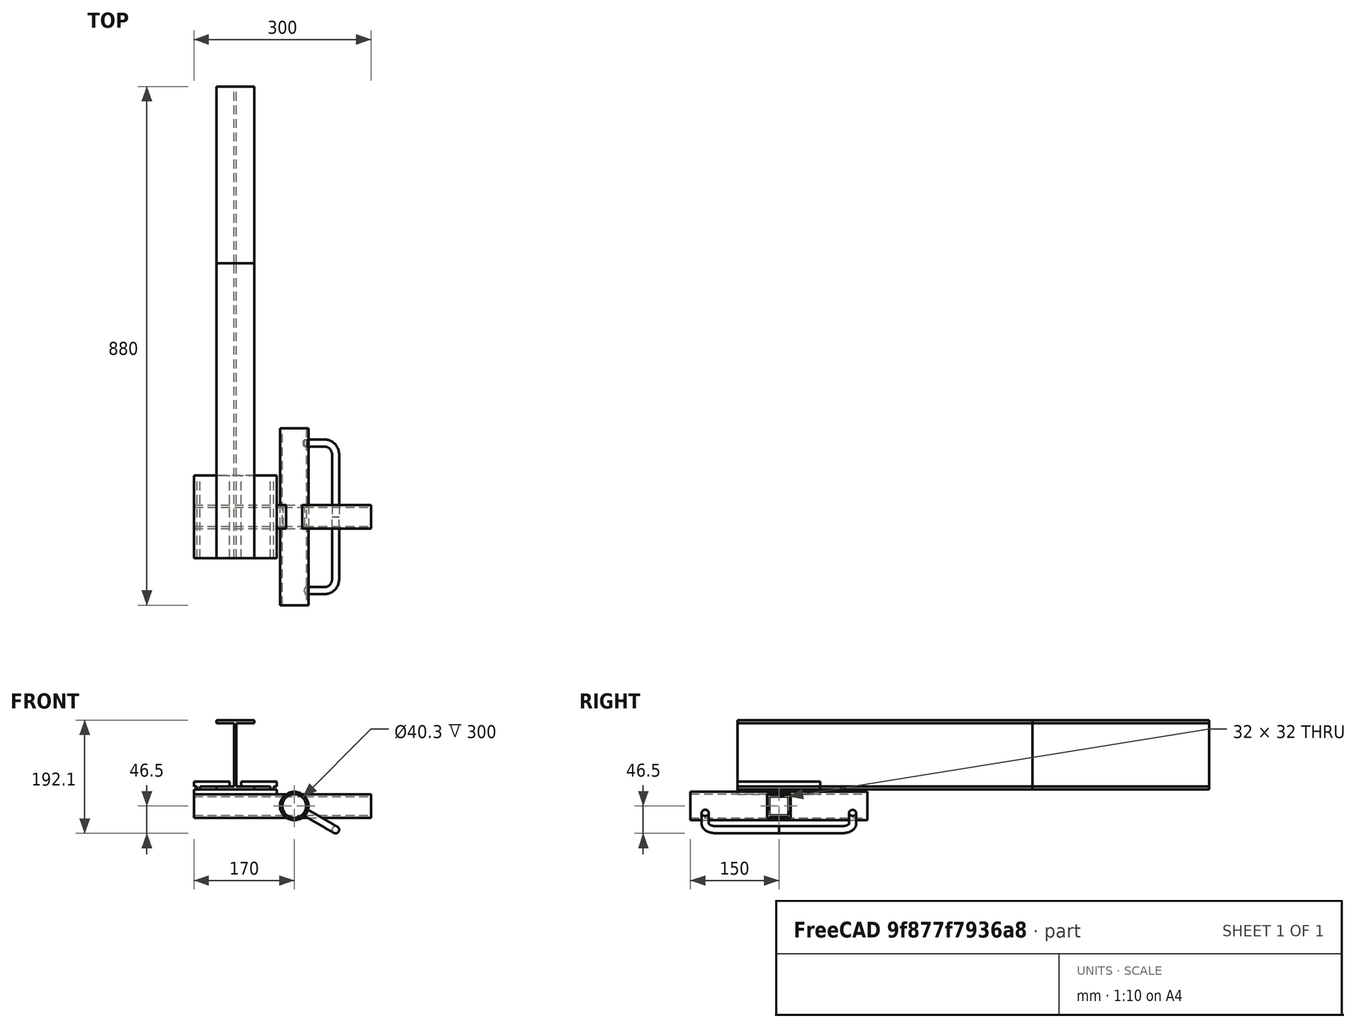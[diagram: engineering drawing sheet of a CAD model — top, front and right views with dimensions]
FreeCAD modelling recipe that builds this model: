
FCSTD DOCUMENT  (FreeCAD 0.21R33771 (Git))
Label: Haltegriff_FEM_RC
License: All rights reserved
LicenseURL: https://en.wikipedia.org/wiki/All_rights_reserved
objects: Part::FeaturePython×8, Sketcher::SketchObject×5, Part::Feature×3, Part::Extrusion×3, Fem::FeaturePython×2, Fem::ConstraintForce×2, Part::Sweep×1, App::DocumentObjectGroup×1, App::MaterialObjectPython×1, Fem::ConstraintFixed×1, Fem::FemSolverObjectPython×1, Fem::FemMeshObjectPython×1, Fem::FemAnalysis×1
note: 20 computed .brp shape members not serialized (recipe doc carries the construction recipe); baked Part::Feature solids carry a one-line shape summary decoded from their .brp

FEATURE [Part::Feature] Defeatured  label="IPEA120"
  shape: bbox 64 x 500 x 117.6 mm, 14 faces (baked)
FEATURE [Part::Feature] Defeatured002  label="IPEA120_2"
  shape: bbox 64 x 300 x 117.6 mm, 14 faces (baked)
FEATURE [Sketcher::SketchObject] Sketch
  ExternalGeometry = -> [Defeatured]
  FullyConstrained = true
  MapMode = 5
  Placement = pos=(0,0,0) rot=(1,0,0;1.5708rad)
  sketch-geometry (4):
    g0: LineSegment StartX=-70 StartY=-58.8 StartZ=0 EndX=-70 EndY=-66.8 EndZ=0
    g1: LineSegment StartX=-70 StartY=-66.8 StartZ=0 EndX=70 EndY=-66.8 EndZ=0
    g2: LineSegment StartX=70 StartY=-66.8 StartZ=0 EndX=70 EndY=-58.8 EndZ=0
    g3: LineSegment StartX=70 StartY=-58.8 StartZ=0 EndX=-70 EndY=-58.8 EndZ=0
  constraints (11):
    c: Coincident(g0,g1)
    c: Coincident(g1,g2)
    c: Coincident(g2,g3)
    c: Coincident(g3,g0)
    c: Vertical(g0)
    c: Vertical(g2)
    c: Horizontal(g3)
    c: Symmetric(g0,g1,g-2)
    c: PointOnObject(g-3,g3)
    c: DistanceY(g2,g2) = 8
    c: DistanceX(g1,g1) = 140
FEATURE [Part::Extrusion] Extrude  label="platte"
  Base = -> Sketch
  Dir = (0,1,0)
  DirMode = 0
  FaceMakerClass = Part::FaceMakerBullseye
  LengthFwd = 140
  LengthRev = 0
  Solid = true
  Symmetric = false
FEATURE [Sketcher::SketchObject] Sketch001
  ExternalGeometry = -> [Extrude,Defeatured]
  FullyConstrained = true
  MapMode = 5
  Placement = pos=(0,0,0) rot=(1,0,0;1.5708rad)
  sketch-geometry (16):
    g0: LineSegment StartX=64.9 StartY=-58.8 StartZ=0 EndX=64.9 EndY=-53.7 EndZ=0
    g1: LineSegment StartX=64.9 StartY=-53.7 StartZ=0 EndX=70 EndY=-53.7 EndZ=0
    g2: LineSegment StartX=70 StartY=-53.7 StartZ=0 EndX=70 EndY=-45.7 EndZ=0
    g3: LineSegment StartX=70 StartY=-45.7 StartZ=0 EndX=10 EndY=-45.7 EndZ=0
    g4: LineSegment StartX=10 StartY=-45.7 StartZ=0 EndX=10 EndY=-53.7 EndZ=0
    g5: LineSegment StartX=10 StartY=-53.7 StartZ=0 EndX=59.8 EndY=-53.7 EndZ=0
    g6: LineSegment StartX=59.8 StartY=-53.7 StartZ=0 EndX=59.8 EndY=-58.8 EndZ=0
    g7: LineSegment StartX=59.8 StartY=-58.8 StartZ=0 EndX=64.9 EndY=-58.8 EndZ=0
    g8: LineSegment StartX=-64.9 StartY=-58.8 StartZ=0 EndX=-64.9 EndY=-53.7 EndZ=0
    g9: LineSegment StartX=-64.9 StartY=-53.7 StartZ=0 EndX=-70 EndY=-53.7 EndZ=0
    g10: LineSegment StartX=-70 StartY=-53.7 StartZ=0 EndX=-70 EndY=-45.7 EndZ=0
    g11: LineSegment StartX=-70 StartY=-45.7 StartZ=0 EndX=-10 EndY=-45.7 EndZ=0
    g12: LineSegment StartX=-10 StartY=-45.7 StartZ=0 EndX=-10 EndY=-53.7 EndZ=0
    g13: LineSegment StartX=-10 StartY=-53.7 StartZ=0 EndX=-59.8 EndY=-53.7 EndZ=0
    g14: LineSegment StartX=-59.8 StartY=-53.7 StartZ=0 EndX=-59.8 EndY=-58.8 EndZ=0
    g15: LineSegment StartX=-59.8 StartY=-58.8 StartZ=0 EndX=-64.9 EndY=-58.8 EndZ=0
  constraints (48):
    c: Coincident(g0,g1)
    c: Coincident(g1,g2)
    c: Vertical(g2)
    c: Coincident(g2,g3)
    c: Horizontal(g3)
    c: Coincident(g3,g4)
    c: Vertical(g4)
    c: Coincident(g4,g5)
    c: Horizontal(g5)
    c: Coincident(g5,g6)
    c: Vertical(g6)
    c: Coincident(g6,g7)
    c: Coincident(g7,g0)
    c: Coincident(g8,g9)
    c: Coincident(g9,g10)
    c: Vertical(g10)
    c: Coincident(g10,g11)
    c: Horizontal(g11)
    c: Coincident(g11,g12)
    c: Coincident(g12,g13)
    c: Horizontal(g13)
    c: Coincident(g13,g14)
    c: Coincident(g14,g15)
    c: Coincident(g15,g8)
    c: Horizontal(g15)
    c: Vertical(g8)
    c: Vertical(g14)
    c: Horizontal(g9)
    c: Horizontal(g8,g13)
    c: PointOnObject(g-6,g13)
    c: Horizontal(g-4,g8)
    c: Vertical(g-4,g9)
    c: Equal(g-4,g10)
    c: Equal(g14,g15)
    c: Equal(g8,g9)
    c: Vertical(g12)
    c: DistanceX(g11,g11) = 60
    c: Horizontal(g7)
    c: Horizontal(g0,g-3)
    c: Vertical(g0)
    c: Horizontal(g0,g5)
    c: PointOnObject(g-5,g5)
    c: Equal(g12,g2)
    c: Equal(g3,g11)
    c: Horizontal(g1)
    c: Vertical(g1,g-3)
    c: Equal(g1,g7)
    c: Equal(g7,g0)
FEATURE [Part::Extrusion] Extrude001  label="platte001"
  Base = -> Sketch001
  Dir = (0,1,0)
  DirMode = 0
  FaceMakerClass = Part::FaceMakerBullseye
  LengthFwd = 140
  LengthRev = 0
  Solid = true
  Symmetric = false
FEATURE [Part::Feature] Defeatured003  label="QR40x4"
  shape: bbox 300 x 40 x 40 mm, 10 faces (baked)
FEATURE [Sketcher::SketchObject] Sketch002
  FullyConstrained = true
  Placement = pos=(0,0,0) rot=(1,0,0;1.5708rad)
  sketch-geometry (3):
    g0: Circle CenterX=0 CenterY=0 CenterZ=0 NormalX=0 NormalY=0 NormalZ=1 AngleXU=0 Radius=24.15
    g1: Circle CenterX=0 CenterY=0 CenterZ=0 NormalX=0 NormalY=0 NormalZ=1 AngleXU=0 Radius=20.15
    g2: LineSegment StartX=20.15 StartY=0 StartZ=0 EndX=24.15 EndY=0 EndZ=0
  constraints (8):
    c: Diameter(g0) = 48.3
    c: Coincident(g0,g-1)
    c: Coincident(g1,g0)
    c: PointOnObject(g2,g1)
    c: PointOnObject(g2,g0)
    c: PointOnObject(g2,g-1)
    c: Horizontal(g2)
    c: DistanceX(g2,g2) = 4
FEATURE [Part::Extrusion] Extrude002  label="R48x4"
  Base = -> Sketch002
  Dir = (0,-1,2e-16)
  DirMode = 2
  FaceMakerClass = Part::FaceMakerBullseye
  LengthFwd = 80
  LengthRev = 220
  Placement = pos=(100,1.42e-14,-86.8) rot=(0,0,1;0rad)
  Solid = true
  Symmetric = false
FEATURE [Sketcher::SketchObject] Sketch003
  ExternalGeometry = -> [Extrude002]
  FullyConstrained = true
  sketch-geometry (10):
    g0: LineSegment StartX=0 StartY=195 StartZ=0 EndX=40 EndY=195 EndZ=0
    g1: LineSegment StartX=0 StartY=-55 StartZ=0 EndX=40 EndY=-55 EndZ=0
    g2: LineSegment StartX=60 StartY=175 StartZ=0 EndX=60 EndY=120 EndZ=0
    g3: LineSegment StartX=60 StartY=20 StartZ=0 EndX=60 EndY=-35 EndZ=0
    g4: ArcOfCircle CenterX=40 CenterY=175 CenterZ=0 NormalX=0 NormalY=0 NormalZ=1 AngleXU=0 Radius=20 StartAngle=0 EndAngle=1.5708
    g5: ArcOfCircle CenterX=40 CenterY=-35 CenterZ=0 NormalX=0 NormalY=0 NormalZ=1 AngleXU=0 Radius=20 StartAngle=4.71239 EndAngle=6.28319
    g6: LineSegment StartX=60 StartY=120 StartZ=0 EndX=60 EndY=70 EndZ=0
    g7: LineSegment StartX=60 StartY=70 StartZ=0 EndX=60 EndY=20 EndZ=0
    g8: LineSegment StartX=120.15 StartY=220 StartZ=0 EndX=0 EndY=195 EndZ=0
    g9: LineSegment StartX=120.15 StartY=-80 StartZ=0 EndX=0 EndY=-55 EndZ=0
  constraints (31):
    c: Horizontal(g0)
    c: Horizontal(g1)
    c: Vertical(g2)
    c: Coincident(g6,g2)
    c: Vertical(g3)
    c: Coincident(g7,g3)
    c: Equal(g2,g3)
    c: DistanceY(g7,g6) = 100
    c: Vertical(g0,g1)
    c: Vertical(g0,g1)
    c: DistanceY(g1,g0) = 250
    c: Coincident(g4,g0)
    c: Coincident(g4,g2)
    c: Coincident(g5,g3)
    c: Coincident(g5,g1)
    c: Vertical(g5,g1)
    c: Horizontal(g5,g3)
    c: Vertical(g4,g0)
    c: Horizontal(g4,g2)
    c: Radius(g4) = 20
    c: DistanceX(g0,g2) = 60
    c: Coincident(g6,g7)
    c: Vertical(g6)
    c: Vertical(g7)
    c: Equal(g6,g7)
    c: PointOnObject(g1,g-2)
    c: Coincident(g8,g-3)
    c: Coincident(g8,g0)
    c: Coincident(g9,g-3)
    c: Coincident(g9,g1)
    c: Equal(g9,g8)
FEATURE [Sketcher::SketchObject] Sketch004
  ExternalGeometry = -> [Sketch003]
  FullyConstrained = true
  Placement = pos=(0,0,0) rot=(0.57735,0.57735,0.57735;2.0944rad)
  sketch-geometry (1):
    g0: Circle CenterX=-55 CenterY=0 CenterZ=0 NormalX=0 NormalY=0 NormalZ=1 AngleXU=0 Radius=6
  constraints (2):
    c: Coincident(g0,g-3)
    c: Diameter(g0) = 12
FEATURE [Part::Sweep] Sweep
  Frenet = true
  Placement = pos=(118.187,1.4e-14,-97.3) rot=(0,1,0;0.523599rad)
  Sections = -> [Sketch004]
  Solid = true
  Spine = -> Sketch003 [Edge1,Edge2,Edge3,Edge4]
  Transition = 1
FEATURE [Part::FeaturePython] Clone  label="Sweep001"  # Draft clone (typed FeaturePython)
  AttacherType = Attacher::AttachEngine3D
  Fuse = false
  Objects = -> [Sweep]
  Placement = pos=(118.187,140,-97.3) rot=(0.965926,0,-0.258819;3.14159rad)
  Scale = (1,1,1)
FEATURE [Part::FeaturePython] Facebinder  # WARN: FeaturePython — macro-defined, semantics opaque (R4)
  Area = 45521.7
  Extrusion = 0
  Faces = -> [Extrude002]
  RemoveSplitter = false
  Sew = false
FEATURE [Part::FeaturePython] Slice  # WARN: FeaturePython — macro-defined, semantics opaque (R4)
  Base = -> Defeatured003
  Mode = 1
  Tolerance = 0
  Tools = -> [Facebinder]
FEATURE [Part::FeaturePython] Slice_child0  label="Slice.0"  # WARN: FeaturePython — macro-defined, semantics opaque (R4)
  Base = -> Slice
  FilterType = 1
  Invert = false
  OverrideMaxVal = 0
  WindowFrom = 80
  WindowTo = 100
  items = 0
FEATURE [Part::FeaturePython] Slice_child1  label="Slice.1"  # WARN: FeaturePython — macro-defined, semantics opaque (R4)
  Base = -> Slice
  FilterType = 1
  Invert = false
  OverrideMaxVal = 0
  WindowFrom = 80
  WindowTo = 100
  items = 1
FEATURE [Part::FeaturePython] Slice_child2  label="Slice.2"  # WARN: FeaturePython — macro-defined, semantics opaque (R4)
  Base = -> Slice
  FilterType = 1
  Invert = false
  OverrideMaxVal = 0
  WindowFrom = 80
  WindowTo = 100
  items = 2
FEATURE [App::DocumentObjectGroup] GrExplode_Slice  label="Exploded Slice"
  Group = -> [Slice_child0,Slice_child1,Slice_child2]
FEATURE [Part::FeaturePython] BooleanFragments  # WARN: FeaturePython — macro-defined, semantics opaque (R4)
  Mode = 2
  Objects = -> [Defeatured,Defeatured002,Extrude,Extrude001,Extrude002,Sweep,Clone,Slice_child0]
  Tolerance = 0
FEATURE [Part::FeaturePython] CompoundFilter  # WARN: FeaturePython — macro-defined, semantics opaque (R4)
  Base = -> BooleanFragments
  FilterType = 3
  Invert = false
  OverrideMaxVal = 0
  WindowFrom = 80
  WindowTo = 100
FEATURE [Fem::FeaturePython] MeshRegion  # FEM object (typed FeaturePython)
  CharacteristicLength = 5
  References = -> [CompoundFilter]
FEATURE [Fem::FeaturePython] MeshRegion001  # FEM object (typed FeaturePython)
  CharacteristicLength = 3
  References = -> [CompoundFilter]
FEATURE [App::MaterialObjectPython] MaterialSolid  label="S235"  # material (typed FeaturePython)
  Category = 0
  Material = AmbientColor=(0.0020, 0.0020, 0.0020, 1.0),Author=Juergen Riegel,AuthorAndLicense=CC-BY-3.0,CardName=CalculiX-Steel,Density=7.9e-06 kg/mm^3,+14 more (map truncated)
  UUID = 92589471-a6cb-4bbc-b748-d425a17dea7d
FEATURE [Fem::ConstraintFixed] ConstraintFixed
  NormalDirection = (0,1,-2e-16)
  Normals = (8) [(0,1,-2.2e-16),(0,1,-2.2e-16),(0,1,-2.2e-16),(0,1,-2.2e-16),(0,1,-2.2e-16),(0,1,-2.2e-16),(0,1,-2.2e-16),(0,1,-2.2e-16)]
  Points = (8) [(-32,800,58.8),(-10.6667,800,58.8),(10.6667,800,58.8),(32,800,58.8),(-32,800,-58.8),(-10.6667,800,-58.8),(10.6667,800,-58.8),(32,800,-58.8)]
  References = -> [CompoundFilter]
  Scale = 9
FEATURE [Fem::ConstraintForce] ConstraintForce  label="Luefter"
  DirectionVector = (0,0,-1)
  Force = 1000
  NormalDirection = (0,0,1)
  Points = (16) [(-32,500,58.8),(-10.6667,500,58.8),(10.6667,500,58.8),(32,500,58.8),(-32,333.333,58.8),(-10.6667,333.333,58.8),(10.6667,333.333,58.8),+9 more]
  References = -> [CompoundFilter]
  Reversed = true
  Scale = 18
FEATURE [Fem::ConstraintForce] ConstraintForce001  label="Mannlast"
  DirectionVector = (0.866025,0,-0.5)
  Force = 1000
  NormalDirection = (0.866025,0,-0.5)
  Points = (16) [(164.952,20,-124.3),(175.344,20,-124.3),(170.148,20,-133.3),(164.952,20,-124.3),(164.952,36.6667,-124.3),(175.344,36.6667,-124.3),+10 more]
  References = -> [CompoundFilter]
  Scale = 5
FEATURE [Fem::FemSolverObjectPython] SolverCcxTools  # FEM object (typed FeaturePython)
  AnalysisType = 0
  BeamReducedIntegration = true
  BeamShellResultOutput3D = true
  BucklingFactors = 1
  EigenmodeHighLimit = 1000000
  EigenmodeLowLimit = 0
  EigenmodesCount = 10
  GeometricalNonlinearity = 0
  IterationsControlParameterCutb = 0.25,0.5,0.75,0.85,,,1.5,
  IterationsControlParameterIter = 4,8,9,200,10,400,,200,,
  IterationsControlParameterTimeUse = false
  IterationsMaximum = 2000
  IterationsThermoMechMaximum = 2000
  IterationsUserDefinedIncrementations = false
  IterationsUserDefinedTimeStepLength = false
  MaterialNonlinearity = 0
  MatrixSolverType = 1
  ModelSpace = 0
  OutputFrequency = 1
  SplitInputWriter = true
  ThermoMechSteadyState = true
  ThermoMechType = 0
  TimeEnd = 1
  TimeInitialStep = 0.01
  TimeMaximumStep = 1
  TimeMinimumStep = 1e-05
FEATURE [Fem::FemMeshObjectPython] FEMMeshGmsh  # FEM object (typed FeaturePython)
  Algorithm2D = 0
  Algorithm3D = 0
  CharacteristicLengthMax = 20
  CharacteristicLengthMin = 0
  CoherenceMesh = true
  ElementDimension = 0
  ElementOrder = 1
  GeometryTolerance = 1e-06
  GroupsOfNodes = false
  HighOrderOptimize = 0
  MeshSizeFromCurvature = 12
  OptimizeNetgen = false
  OptimizeStd = true
  Part = -> CompoundFilter
  RecombinationAlgorithm = 0
  Recombine3DAll = false
  RecombineAll = false
  SecondOrderLinear = false
FEATURE [Fem::FemAnalysis] Analysis
  Group = -> [MaterialSolid,ConstraintFixed,ConstraintForce,ConstraintForce001,SolverCcxTools,FEMMeshGmsh]
